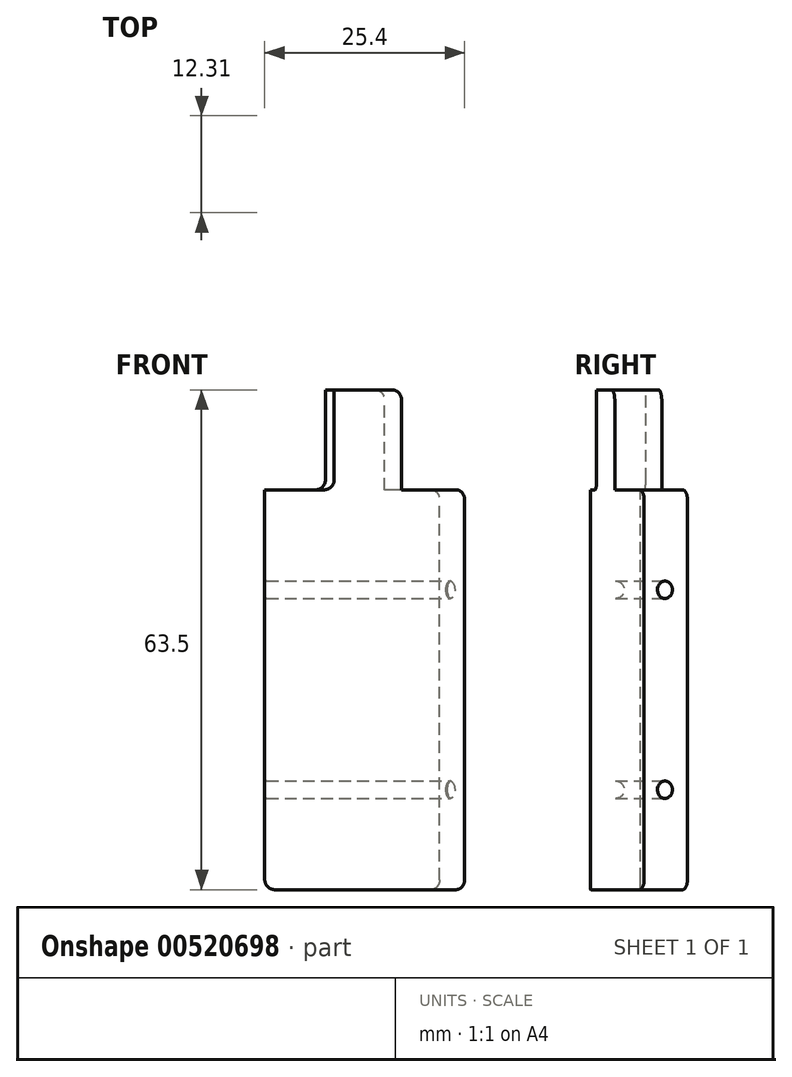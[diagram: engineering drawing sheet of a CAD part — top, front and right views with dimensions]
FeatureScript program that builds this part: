
annotation { "Feature Type Name" : "Feature", "Feature Type Description" : "" }
export const myFeature = defineFeature(function(context is Context, id is Id, definition is map)
    precondition{}
    {
        {
            var Q0;
            Q0=qCreatedBy(makeId("Right.planeOp"),FACE);
            var sketch = newSketch(context, id + "F0", { "sketchPlane" : qUnion([Q0])});
            skLineSegment(sketch, "E0.right", {"start": v(-50.8, 0) * mm, "end": v(-50.8, 50.8) * mm});
            skLineSegment(sketch, "E1", {"start": v(-50.8, 0) * mm, "end": v(-44.45, 0) * mm});
            skLineSegment(sketch, "E2", {"start": v(-50.8, 50.8) * mm, "end": v(-44.45, 50.8) * mm});
            skLineSegment(sketch, "E3", {"start": v(-44.45, 0) * mm, "end": v(-44.45, 50.8) * mm});
            skSolve(sketch);
        }
        {
            var Q0;
            Q0=qCreatedBy(makeId("Right.planeOp"),FACE);
            var sketch = newSketch(context, id + "F1", { "sketchPlane" : qUnion([Q0])});
            skLineSegment(sketch, "E4", {"start": v(0, 0) * mm, "end": v(0, 58.6) * mm});
            skSolve(sketch);
        }
        {
            var Q0;
            Q0=makeQuery(id+"F0.imprint","IMPRINT",FACE,{"disambiguationData":[TD([[makeQuery(id+"F0.imprint","IMPRINT",EDGE,{"derivedFrom":sQuery(id+"F0.wireOp",EDGE,"E0.right")}),-1.0]])]});
            var Q1;
            Q1=sQuery(id+"F1.wireOp",EDGE,"E4");
            revolve(context, id + "F2", {"entities" : qUnion([Q0]), "axis" : qUnion([Q1]), "revolveType" : RevolveType.ONE_DIRECTION, "angle" : 30 * degree});
        }
        {
            var Q0;
            Q0=qCreatedBy(makeId("Right.planeOp"),FACE);
            var sketch = newSketch(context, id + "F3", { "sketchPlane" : qUnion([Q0])});
            skLineSegment(sketch, "E5", {"start": v(-50.8, 50.8) * mm, "end": v(-44.45, 50.8) * mm});
            skLineSegment(sketch, "E6", {"start": v(-44.45, 50.8) * mm, "end": v(-44.45, 63.5) * mm});
            skLineSegment(sketch, "E7", {"start": v(-50.8, 50.8) * mm, "end": v(-50.8, 63.5) * mm});
            skLineSegment(sketch, "E8", {"start": v(-50.8, 63.5) * mm, "end": v(-44.45, 63.5) * mm});
            skSolve(sketch);
        }
        {
            var Q0;
            Q0 = qSketchRegion(id + "F3", true);
            var Q1;
            Q1=sQuery(id+"F1.wireOp",EDGE,"E4");
            revolve(context, id + "F4", {"operationType" : NewBodyOperationType.ADD, "entities" : qUnion([Q0]), "axis" : qUnion([Q1]), "revolveType" : RevolveType.ONE_DIRECTION, "angle" : 20 * degree});
        }
        {
            var Q0;
            Q0 = qSketchRegion(id + "F3", true);
            var Q1;
            Q1=sQuery(id+"F1.wireOp",EDGE,"E4");
            revolve(context, id + "F5", {"operationType" : NewBodyOperationType.REMOVE, "entities" : qUnion([Q0]), "axis" : qUnion([Q1]), "revolveType" : RevolveType.ONE_DIRECTION, "angle" : 10 * degree});
        }
        {
            var Q0;
            Q0=makeQuery(id+"F4.opRevolve","CAP_EDGE",EDGE,{"disambiguationData":[OSD([sQuery(id+"F3.wireOp",EDGE,"E8")])],"isStart":false});
            var Q1;
            Q1=makeQuery(id+"F5.boolean.opBoolean","COPY",EDGE,{"derivedFrom":makeQuery(id+"F5.opRevolve","CAP_EDGE",EDGE,{"disambiguationData":[OSD([sQuery(id+"F3.wireOp",EDGE,"E8")])],"isStart":false})});
            var Q2;
            Q2=makeQuery(id+"F2.opRevolve","CAP_EDGE",EDGE,{"disambiguationData":[OSD([sQuery(id+"F0.wireOp",EDGE,"E2")])],"isStart":false});
            var Q3;
            Q3=makeQuery(id+"F5.boolean.opBoolean","COPY",EDGE,{"derivedFrom":makeQuery(id+"F5.opRevolve","CAP_EDGE",EDGE,{"disambiguationData":[OSD([sQuery(id+"F3.wireOp",EDGE,"E5")])],"isStart":false})});
            var Q4;
            Q4=makeQuery(id+"F2.opRevolve","CAP_EDGE",EDGE,{"disambiguationData":[OSD([sQuery(id+"F0.wireOp",EDGE,"E1")])],"isStart":true});
            var Q5;
            Q5=makeQuery(id+"F2.opRevolve","CAP_EDGE",EDGE,{"disambiguationData":[OSD([sQuery(id+"F0.wireOp",EDGE,"E1")])],"isStart":false});
            var Q6;
            Q6=makeQuery(id+"F4.opRevolve","CAP_EDGE",EDGE,{"disambiguationData":[OSD([sQuery(id+"F3.wireOp",EDGE,"E5")])],"isStart":false});
            var Q7;
            Q7=makeQuery(id+"F5.boolean.opBoolean","COPY",EDGE,{"derivedFrom":makeQuery(id+"F5.opRevolve","CAP_EDGE",EDGE,{"disambiguationData":[OSD([sQuery(id+"F3.wireOp",EDGE,"E5")])],"isStart":true})});
            fillet(context, id + "F6", {"entities" : qUnion([Q0, Q1, Q2, Q3, Q4, Q5, Q6, Q7]), "radius" : 1.27 * mm, "tangentPropagation" : true, "allowEdgeOverflow" : false});
        }
        {
            var Q0;
            Q0=qCreatedBy(makeId("Right.planeOp"),FACE);
            var sketch = newSketch(context, id + "F7", { "sketchPlane" : qUnion([Q0])});
            skPoint(sketch, "E9", {"position": v(-47.63, 12.7) * mm});
            skPoint(sketch, "E10", {"position": v(-47.63, 38.1) * mm});
            skCircle(sketch, "E11", {"center": v(-47.63, 38.1) * mm, "radius": 1.11 * mm});
            skCircle(sketch, "E12", {"center": v(-47.63, 12.7) * mm, "radius": 1.11 * mm});
            skSolve(sketch);
        }
        {
            var Q0;
            Q0 = qSketchRegion(id + "F7", true);
            var Q1;
            Q1=sQuery(id+"F1.wireOp",EDGE,"E4");
            revolve(context, id + "F8", {"operationType" : NewBodyOperationType.REMOVE, "entities" : qUnion([Q0]), "axis" : qUnion([Q1]), "revolveType" : RevolveType.FULL, "oppositeDirection" : true});
        }
        {
            var Q0;
            Q0=makeQuery(id+"F8.boolean.opBoolean","INTERSECT",EDGE,{"derivedFrom":[makeQuery(id+"F2.opRevolve","CAP_FACE",FACE,{"disambiguationData":[OSD([sQuery(id+"F0.wireOp",EDGE,"E0.right"),sQuery(id+"F0.wireOp",EDGE,"E1"),sQuery(id+"F0.wireOp",EDGE,"E2"),sQuery(id+"F0.wireOp",EDGE,"E3")])],"isStart":false}),makeQuery(id+"F8.opRevolve","SWEPT_FACE",FACE,{"disambiguationData":[OSD([sQuery(id+"F7.wireOp",EDGE,"E11")])]})]});
            var Q1;
            Q1=makeQuery(id+"F8.boolean.opBoolean","INTERSECT",EDGE,{"derivedFrom":[makeQuery(id+"F2.opRevolve","CAP_FACE",FACE,{"disambiguationData":[OSD([sQuery(id+"F0.wireOp",EDGE,"E0.right"),sQuery(id+"F0.wireOp",EDGE,"E1"),sQuery(id+"F0.wireOp",EDGE,"E2"),sQuery(id+"F0.wireOp",EDGE,"E3")])],"isStart":false}),makeQuery(id+"F8.opRevolve","SWEPT_FACE",FACE,{"disambiguationData":[OSD([sQuery(id+"F7.wireOp",EDGE,"E12")])]})]});
            var Q2;
            Q2=makeQuery(id+"F8.boolean.opBoolean","INTERSECT",EDGE,{"derivedFrom":[makeQuery(id+"F4.boolean.opBoolean","MERGE",FACE,{"derivedFrom":[makeQuery(id+"F2.opRevolve","CAP_FACE",FACE,{"disambiguationData":[OSD([sQuery(id+"F0.wireOp",EDGE,"E0.right"),sQuery(id+"F0.wireOp",EDGE,"E1"),sQuery(id+"F0.wireOp",EDGE,"E2"),sQuery(id+"F0.wireOp",EDGE,"E3")])],"isStart":true}),makeQuery(id+"F4.opRevolve","CAP_FACE",FACE,{"disambiguationData":[OSD([sQuery(id+"F3.wireOp",EDGE,"E5"),sQuery(id+"F3.wireOp",EDGE,"E6"),sQuery(id+"F3.wireOp",EDGE,"E7"),sQuery(id+"F3.wireOp",EDGE,"E8")])],"isStart":true})]}),makeQuery(id+"F8.opRevolve","SWEPT_FACE",FACE,{"disambiguationData":[OSD([sQuery(id+"F7.wireOp",EDGE,"E11")])]})]});
            var Q3;
            Q3=makeQuery(id+"F8.boolean.opBoolean","INTERSECT",EDGE,{"derivedFrom":[makeQuery(id+"F4.boolean.opBoolean","MERGE",FACE,{"derivedFrom":[makeQuery(id+"F2.opRevolve","CAP_FACE",FACE,{"disambiguationData":[OSD([sQuery(id+"F0.wireOp",EDGE,"E0.right"),sQuery(id+"F0.wireOp",EDGE,"E1"),sQuery(id+"F0.wireOp",EDGE,"E2"),sQuery(id+"F0.wireOp",EDGE,"E3")])],"isStart":true}),makeQuery(id+"F4.opRevolve","CAP_FACE",FACE,{"disambiguationData":[OSD([sQuery(id+"F3.wireOp",EDGE,"E5"),sQuery(id+"F3.wireOp",EDGE,"E6"),sQuery(id+"F3.wireOp",EDGE,"E7"),sQuery(id+"F3.wireOp",EDGE,"E8")])],"isStart":true})]}),makeQuery(id+"F8.opRevolve","SWEPT_FACE",FACE,{"disambiguationData":[OSD([sQuery(id+"F7.wireOp",EDGE,"E12")])]})]});
            fillet(context, id + "F9", {"entities" : qUnion([Q0, Q1, Q2, Q3]), "radius" : 0.25 * mm, "tangentPropagation" : true, "allowEdgeOverflow" : false});
        }
    });
